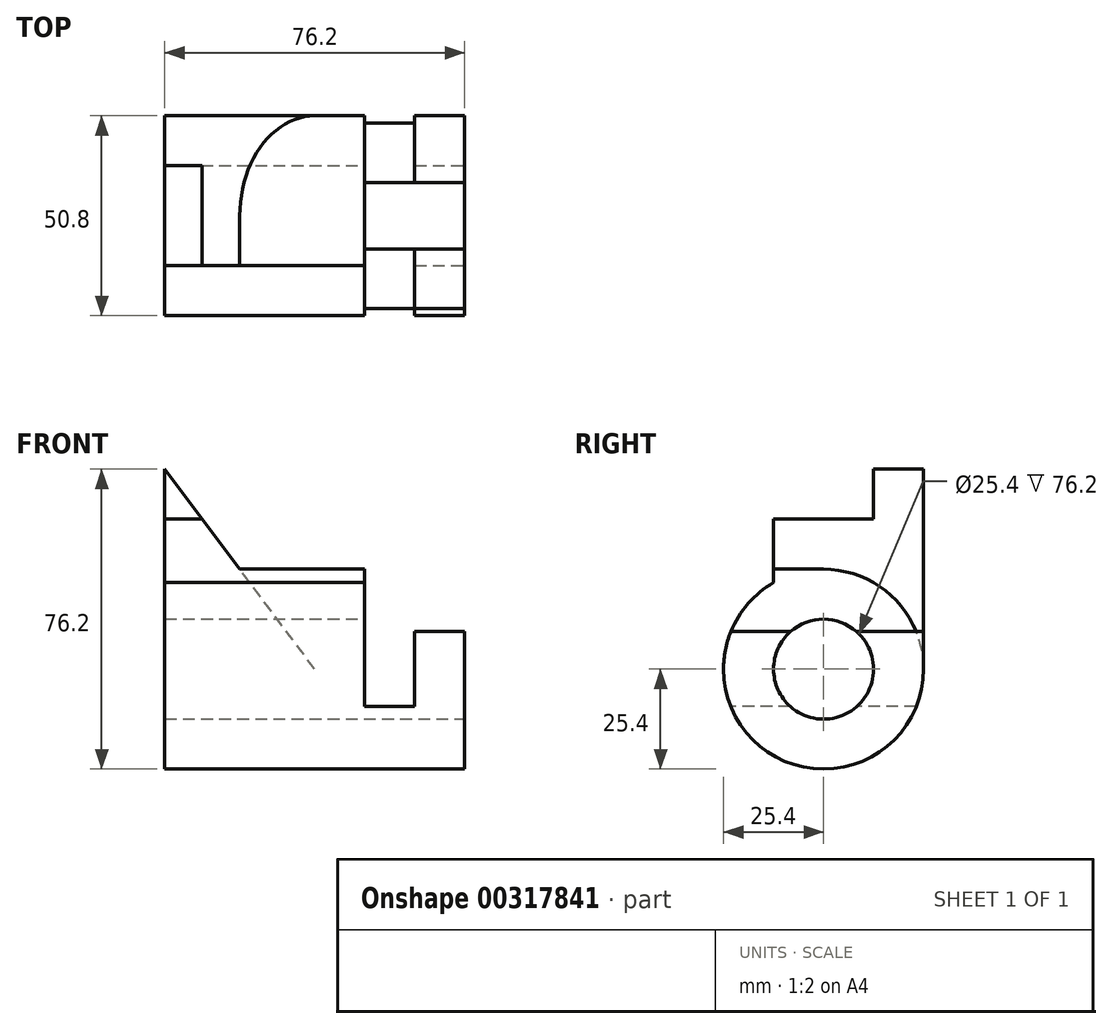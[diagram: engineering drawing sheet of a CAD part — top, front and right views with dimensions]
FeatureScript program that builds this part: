
annotation { "Feature Type Name" : "Feature", "Feature Type Description" : "" }
export const myFeature = defineFeature(function(context is Context, id is Id, definition is map)
    precondition{}
    {
        {
            var Q0;
            Q0=qCreatedBy(makeId("Front.planeOp"),FACE);
            var sketch = newSketch(context, id + "F0", { "sketchPlane" : qUnion([Q0])});
            skLineSegment(sketch, "E0.bottom", {"start": v(0, 0) * mm, "end": v(76.2, 0) * mm});
            skLineSegment(sketch, "E0.top", {"start": v(0, 76.2) * mm, "end": v(76.2, 76.2) * mm});
            skLineSegment(sketch, "E0.left", {"start": v(0, 0) * mm, "end": v(0, 76.2) * mm});
            skLineSegment(sketch, "E0.right", {"start": v(76.2, 0) * mm, "end": v(76.2, 76.2) * mm});
            skSolve(sketch);
        }
        {
            var Q0;
            Q0 = qSketchRegion(id + "F0", true);
            extrude(context, id + "F1", {"entities" : qUnion([Q0]), "depth" : 50.8 * mm});
        }
        {
            var Q0;
            Q0=makeQuery(id+"F1.opExtrude","SWEPT_FACE",FACE,{"disambiguationData":[OSD([sQuery(id+"F0.wireOp",EDGE,"E0.right")])]});
            var sketch = newSketch(context, id + "F2", { "sketchPlane" : qUnion([Q0])});
            skCircle(sketch, "E1", {"center": v(-25.4, 25.4) * mm, "radius": 12.7 * mm});
            skSolve(sketch);
        }
        {
            var Q0;
            Q0 = qSketchRegion(id + "F2", true);
            extrude(context, id + "F3", {"entities" : qUnion([Q0]), "operationType" : NewBodyOperationType.REMOVE, "endBound" : BoundingType.THROUGH_ALL, "oppositeDirection" : true, "depth" : 25.4 * mm});
        }
        {
            var Q0;
            Q0=makeQuery(id+"F1.opExtrude","CAP_FACE",FACE,{"disambiguationData":[OSD([sQuery(id+"F0.wireOp",EDGE,"E0.bottom"),sQuery(id+"F0.wireOp",EDGE,"E0.top"),sQuery(id+"F0.wireOp",EDGE,"E0.left"),sQuery(id+"F0.wireOp",EDGE,"E0.right")])],"isStart":false});
            var sketch = newSketch(context, id + "F4", { "sketchPlane" : qUnion([Q0])});
            skLineSegment(sketch, "E2", {"start": v(76.2, 34.93) * mm, "end": v(63.5, 34.93) * mm});
            skLineSegment(sketch, "E3", {"start": v(63.5, 34.93) * mm, "end": v(63.5, 15.88) * mm});
            skLineSegment(sketch, "E4", {"start": v(63.5, 15.88) * mm, "end": v(50.8, 15.88) * mm});
            skLineSegment(sketch, "E5", {"start": v(50.8, 15.88) * mm, "end": v(50.8, 50.8) * mm});
            skLineSegment(sketch, "E6", {"start": v(50.8, 50.8) * mm, "end": v(19.05, 50.8) * mm});
            skLineSegment(sketch, "E7", {"start": v(0, 76.2) * mm, "end": v(38.1, 25.4) * mm, "construction": true});
            skLineSegment(sketch, "E8", {"start": v(19.05, 50.8) * mm, "end": v(0, 76.2) * mm});
            skLineSegment(sketch, "E9", {"start": v(0, 76.2) * mm, "end": v(76.2, 76.2) * mm});
            skLineSegment(sketch, "E10", {"start": v(76.2, 76.2) * mm, "end": v(76.2, 34.93) * mm});
            skSolve(sketch);
        }
        {
            var Q0;
            Q0 = qSketchRegion(id + "F4", true);
            extrude(context, id + "F5", {"entities" : qUnion([Q0]), "operationType" : NewBodyOperationType.REMOVE, "oppositeDirection" : true, "depth" : 25.4 * mm});
        }
        {
            var Q0;
            Q0 = qSketchRegion(id + "F4", true);
            extrude(context, id + "F6", {"entities" : qUnion([Q0]), "operationType" : NewBodyOperationType.REMOVE, "endBound" : BoundingType.THROUGH_ALL, "oppositeDirection" : true, "depth" : 25.4 * mm});
        }
        {
            var Q0;
            Q0=makeQuery(id+"F5.boolean.opBoolean","COPY",EDGE,{"derivedFrom":makeQuery(id+"F5.opExtrude","CAP_EDGE",EDGE,{"disambiguationData":[OSD([sQuery(id+"F4.wireOp",EDGE,"E6")])],"isStart":true})});
            var Q1;
            Q1=makeQuery(id+"F6.boolean.opBoolean","INTERSECT",EDGE,{"derivedFrom":[makeQuery(id+"F1.opExtrude","CAP_FACE",FACE,{"disambiguationData":[OSD([sQuery(id+"F0.wireOp",EDGE,"E0.bottom"),sQuery(id+"F0.wireOp",EDGE,"E0.top"),sQuery(id+"F0.wireOp",EDGE,"E0.left"),sQuery(id+"F0.wireOp",EDGE,"E0.right")])],"isStart":true}),makeQuery(id+"F6.opExtrude","SWEPT_FACE",FACE,{"disambiguationData":[OSD([sQuery(id+"F4.wireOp",EDGE,"E6")])]})]});
            fillet(context, id + "F7", {"entities" : qUnion([Q0, Q1]), "radius" : 25.4 * mm, "tangentPropagation" : true, "allowEdgeOverflow" : false});
        }
        {
            var Q0;
            Q0=makeQuery(id+"F1.opExtrude","SWEPT_FACE",FACE,{"disambiguationData":[OSD([sQuery(id+"F0.wireOp",EDGE,"E0.left")])]});
            var sketch = newSketch(context, id + "F8", { "sketchPlane" : qUnion([Q0])});
            skLineSegment(sketch, "E11", {"start": v(12.7, 76.2) * mm, "end": v(12.7, 63.6) * mm});
            skLineSegment(sketch, "E12", {"start": v(12.7, 63.6) * mm, "end": v(38.1, 63.6) * mm});
            skLineSegment(sketch, "E13", {"start": v(38.1, 63.6) * mm, "end": v(38.1, 47.4) * mm});
            skLineSegment(sketch, "E14", {"start": v(50.8, 25.4) * mm, "end": v(50.8, 76.2) * mm});
            skLineSegment(sketch, "E15", {"start": v(50.8, 76.2) * mm, "end": v(12.7, 76.2) * mm});
            skArc(sketch, "E16", {"start": v(50.8, 25.4) * mm, "mid": v(47.4, 38.1) * mm, "end": v(38.1, 47.4) * mm});
            skSolve(sketch);
        }
        {
            var Q0;
            Q0 = qSketchRegion(id + "F8", true);
            extrude(context, id + "F9", {"entities" : qUnion([Q0]), "operationType" : NewBodyOperationType.REMOVE, "oppositeDirection" : true, "depth" : 25.4 * mm});
        }
        {
            var Q0;
            Q0 = qSketchRegion(id + "F8", true);
            extrude(context, id + "F10", {"entities" : qUnion([Q0]), "operationType" : NewBodyOperationType.REMOVE, "endBound" : BoundingType.THROUGH_ALL, "oppositeDirection" : true, "depth" : 25.4 * mm});
        }
        {
            var Q0;
            Q0=makeQuery(id+"F1.opExtrude","CAP_EDGE",EDGE,{"disambiguationData":[OSD([sQuery(id+"F0.wireOp",EDGE,"E0.bottom")])],"isStart":false});
            var Q1;
            Q1=makeQuery(id+"F1.opExtrude","CAP_EDGE",EDGE,{"disambiguationData":[OSD([sQuery(id+"F0.wireOp",EDGE,"E0.bottom")])],"isStart":true});
            fillet(context, id + "F11", {"entities" : qUnion([Q0, Q1]), "radius" : 25.4 * mm, "tangentPropagation" : true, "allowEdgeOverflow" : false});
        }
    });
